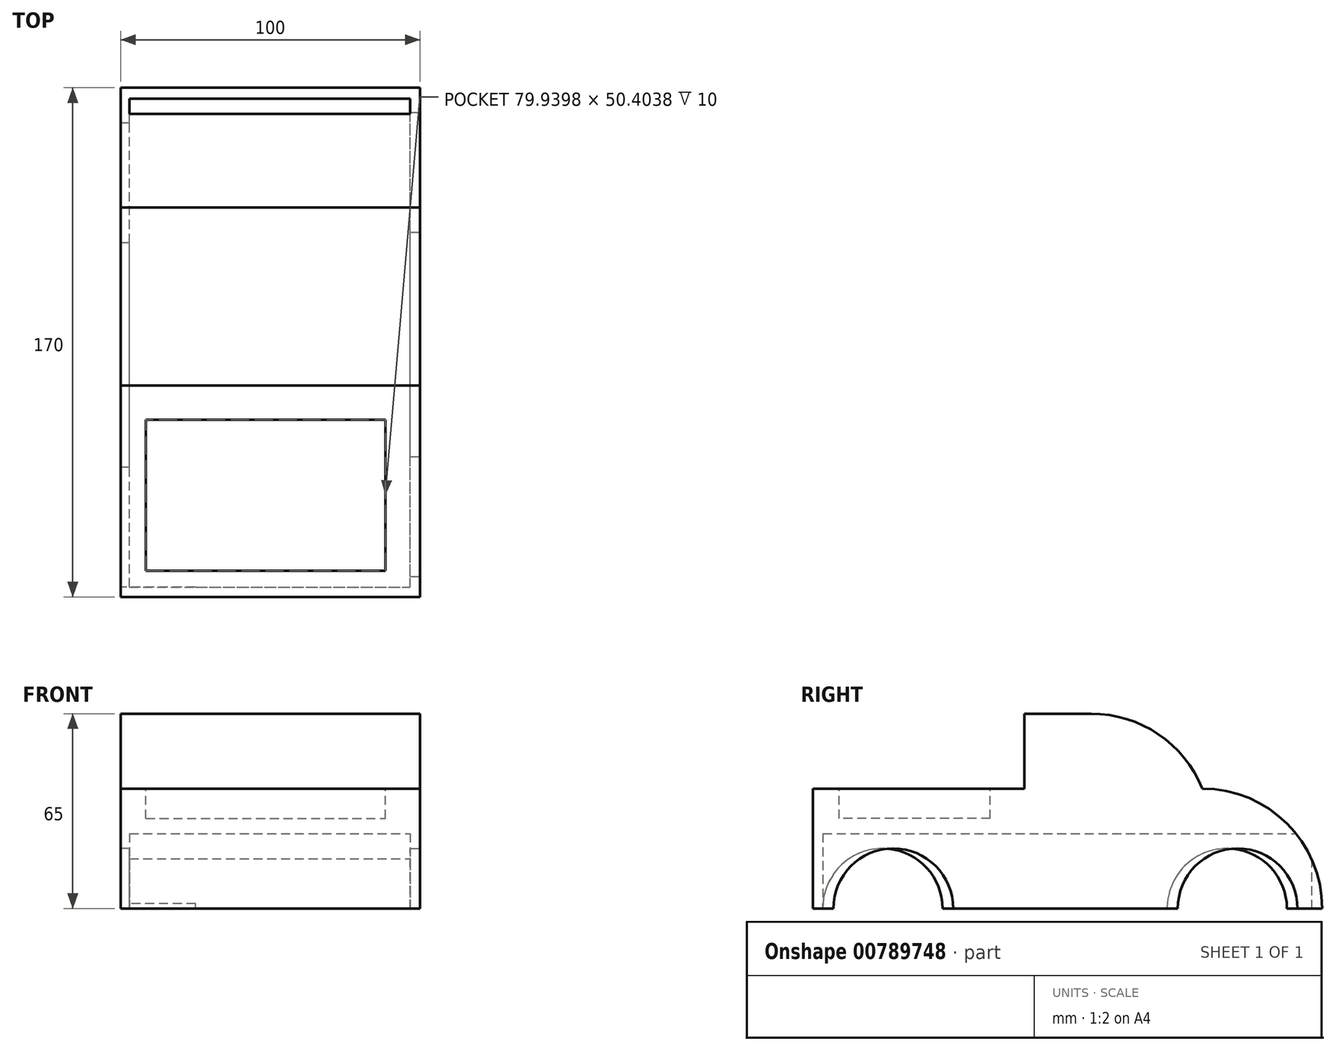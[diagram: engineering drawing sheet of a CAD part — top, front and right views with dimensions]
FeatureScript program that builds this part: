
annotation { "Feature Type Name" : "Feature", "Feature Type Description" : "" }
export const myFeature = defineFeature(function(context is Context, id is Id, definition is map)
    precondition{}
    {
        {
            var Q0;
            Q0=qCreatedBy(makeId("Top.planeOp"),FACE);
            var sketch = newSketch(context, id + "F0", { "sketchPlane" : qUnion([Q0])});
            skLineSegment(sketch, "E0.bottom", {"start": v(-50, 88.78) * mm, "end": v(50, 88.78) * mm});
            skLineSegment(sketch, "E0.top", {"start": v(-50, -81.22) * mm, "end": v(50, -81.22) * mm});
            skLineSegment(sketch, "E0.left", {"start": v(-50, 88.78) * mm, "end": v(-50, -81.22) * mm});
            skLineSegment(sketch, "E0.right", {"start": v(50, 88.78) * mm, "end": v(50, -81.22) * mm});
            skSolve(sketch);
        }
        {
            var Q0;
            Q0=makeQuery(id+"F0.imprint","IMPRINT",FACE,{"disambiguationData":[TD([[makeQuery(id+"F0.imprint","IMPRINT",EDGE,{"derivedFrom":sQuery(id+"F0.wireOp",EDGE,"E0.bottom")}),-1.0]])]});
            extrude(context, id + "F1", {"entities" : qUnion([Q0]), "depth" : 40 * mm, "offsetDistance" : 25 * mm});
        }
        {
            var Q0;
            Q0=makeQuery(id+"F1.opExtrude","CAP_EDGE",EDGE,{"disambiguationData":[OSD([sQuery(id+"F0.wireOp",EDGE,"E0.bottom")])],"isStart":false});
            fillet(context, id + "F2", {"entities" : qUnion([Q0]), "radius" : 40 * mm, "tangentPropagation" : true, "allowEdgeOverflow" : false});
        }
        {
            var Q0;
            Q0=makeQuery(id+"F1.opExtrude","CAP_FACE",FACE,{"disambiguationData":[OSD([sQuery(id+"F0.wireOp",EDGE,"E0.bottom"),sQuery(id+"F0.wireOp",EDGE,"E0.top"),sQuery(id+"F0.wireOp",EDGE,"E0.left"),sQuery(id+"F0.wireOp",EDGE,"E0.right")])],"isStart":false});
            var sketch = newSketch(context, id + "F3", { "sketchPlane" : qUnion([Q0])});
            skLineSegment(sketch, "E1.bottom", {"start": v(-50, 48.78) * mm, "end": v(50, 48.78) * mm});
            skLineSegment(sketch, "E1.top", {"start": v(-50, -10.63) * mm, "end": v(50, -10.63) * mm});
            skLineSegment(sketch, "E1.left", {"start": v(-50, 48.78) * mm, "end": v(-50, -10.63) * mm});
            skLineSegment(sketch, "E1.right", {"start": v(50, 48.78) * mm, "end": v(50, -10.63) * mm});
            skSolve(sketch);
        }
        {
            var Q0;
            Q0=makeQuery(id+"F3.imprint","IMPRINT",FACE,{"disambiguationData":[TD([[makeQuery(id+"F3.imprint","IMPRINT",EDGE,{"derivedFrom":sQuery(id+"F3.wireOp",EDGE,"E1.bottom")}),1.0]])]});
            extrude(context, id + "F4", {"entities" : qUnion([Q0]), "operationType" : NewBodyOperationType.ADD, "depth" : 25 * mm, "offsetDistance" : 25 * mm});
        }
        {
            var Q0;
            Q0=makeQuery(id+"F4.opExtrude","CAP_EDGE",EDGE,{"disambiguationData":[OSD([sQuery(id+"F3.wireOp",EDGE,"E1.bottom")])],"isStart":false});
            fillet(context, id + "F5", {"entities" : qUnion([Q0]), "radius" : 40 * mm, "tangentPropagation" : true, "allowEdgeOverflow" : false});
        }
        {
            var Q0;
            Q0=makeQuery(id+"F4.boolean.opBoolean","MERGE",FACE,{"derivedFrom":[makeQuery(id+"F1.opExtrude","SWEPT_FACE",FACE,{"disambiguationData":[OSD([sQuery(id+"F0.wireOp",EDGE,"E0.right")])]}),makeQuery(id+"F4.opExtrude","SWEPT_FACE",FACE,{"disambiguationData":[OSD([sQuery(id+"F3.wireOp",EDGE,"E1.right")])]})]});
            var sketch = newSketch(context, id + "F6", { "sketchPlane" : qUnion([Q0])});
            skCircle(sketch, "E2", {"center": v(-54.43, 0) * mm, "radius": 20 * mm});
            skCircle(sketch, "E3", {"center": v(60.57, 0) * mm, "radius": 20 * mm});
            skSolve(sketch);
        }
        {
            var Q0;
            {var subQ0=sQuery(id+"F6.wireOp",EDGE,"E2");var subQ1=makeQuery(id+"F1.opExtrude","CAP_EDGE",EDGE,{"disambiguationData":[OSD([sQuery(id+"F0.wireOp",EDGE,"E0.right")])],"isStart":true});var subQ2=makeQuery(id+"F6.imprint","INTERSECT",VERTEX,{"disambiguationData":[OD(0.0)],"derivedFrom":[subQ1,subQ0]});Q0=makeQuery(id+"F6.imprint","IMPRINT",FACE,{"disambiguationData":[TD([[makeQuery(id+"F6.imprint","IMPRINT",EDGE,{"disambiguationData":[TD([[subQ2,1.0]])],"derivedFrom":subQ0}),1.0]])]});}
            var Q1;
            {var subQ0=sQuery(id+"F6.wireOp",EDGE,"E3");var subQ1=makeQuery(id+"F1.opExtrude","CAP_EDGE",EDGE,{"disambiguationData":[OSD([sQuery(id+"F0.wireOp",EDGE,"E0.right")])],"isStart":true});var subQ2=makeQuery(id+"F6.imprint","INTERSECT",VERTEX,{"disambiguationData":[OD(0.0)],"derivedFrom":[subQ1,subQ0]});Q1=makeQuery(id+"F6.imprint","IMPRINT",FACE,{"disambiguationData":[TD([[makeQuery(id+"F6.imprint","IMPRINT",EDGE,{"disambiguationData":[TD([[subQ2,-1.0]])],"derivedFrom":subQ0}),1.0]])]});}
            extrude(context, id + "F7", {"entities" : qUnion([Q0, Q1]), "operationType" : NewBodyOperationType.REMOVE, "oppositeDirection" : true, "depth" : 25 * mm, "offsetDistance" : 25 * mm});
        }
        {
            var Q0;
            Q0=makeQuery(id+"F1.opExtrude","CAP_FACE",FACE,{"disambiguationData":[OSD([sQuery(id+"F0.wireOp",EDGE,"E0.bottom"),sQuery(id+"F0.wireOp",EDGE,"E0.top"),sQuery(id+"F0.wireOp",EDGE,"E0.left"),sQuery(id+"F0.wireOp",EDGE,"E0.right")])],"isStart":true});
            var sketch = newSketch(context, id + "F8", { "sketchPlane" : qUnion([Q0])});
            skLineSegment(sketch, "E4.bottom", {"start": v(-47.03, 77.92) * mm, "end": v(46.71, 77.92) * mm});
            skLineSegment(sketch, "E4.top", {"start": v(-47.03, -85.17) * mm, "end": v(46.71, -85.17) * mm});
            skLineSegment(sketch, "E4.left", {"start": v(-47.03, 77.92) * mm, "end": v(-47.03, -85.17) * mm});
            skLineSegment(sketch, "E4.right", {"start": v(46.71, 77.92) * mm, "end": v(46.71, -85.17) * mm});
            skSolve(sketch);
        }
        {
            var Q0;
            Q0 = qSketchRegion(id + "F8", true);
            extrude(context, id + "F9", {"entities" : qUnion([Q0]), "operationType" : NewBodyOperationType.REMOVE, "oppositeDirection" : true, "depth" : 25 * mm, "offsetDistance" : 25 * mm});
        }
        {
            var Q0;
            Q0=makeQuery(id+"F4.boolean.opBoolean","MERGE",FACE,{"derivedFrom":[makeQuery(id+"F1.opExtrude","SWEPT_FACE",FACE,{"disambiguationData":[OSD([sQuery(id+"F0.wireOp",EDGE,"E0.left")])]}),makeQuery(id+"F4.opExtrude","SWEPT_FACE",FACE,{"disambiguationData":[OSD([sQuery(id+"F3.wireOp",EDGE,"E1.left")])]})]});
            var sketch = newSketch(context, id + "F10", { "sketchPlane" : qUnion([Q0])});
            skCircle(sketch, "E5", {"center": v(-57.01, 0) * mm, "radius": 20 * mm});
            skCircle(sketch, "E6", {"center": v(57.99, 0) * mm, "radius": 20 * mm});
            skSolve(sketch);
        }
        {
            var Q0;
            {var subQ0=sQuery(id+"F10.wireOp",EDGE,"E5");var subQ1=makeQuery(id+"F1.opExtrude","CAP_EDGE",EDGE,{"disambiguationData":[OSD([sQuery(id+"F0.wireOp",EDGE,"E0.left")])],"isStart":true});var subQ2=makeQuery(id+"F10.imprint","INTERSECT",VERTEX,{"disambiguationData":[OD(0.0)],"derivedFrom":[subQ1,subQ0]});Q0=makeQuery(id+"F10.imprint","IMPRINT",FACE,{"disambiguationData":[TD([[makeQuery(id+"F10.imprint","IMPRINT",EDGE,{"disambiguationData":[TD([[subQ2,-1.0]])],"derivedFrom":subQ0}),1.0]])]});}
            var Q1;
            {var subQ0=sQuery(id+"F10.wireOp",EDGE,"E6");var subQ1=makeQuery(id+"F1.opExtrude","CAP_EDGE",EDGE,{"disambiguationData":[OSD([sQuery(id+"F0.wireOp",EDGE,"E0.left")])],"isStart":true});var subQ2=makeQuery(id+"F10.imprint","INTERSECT",VERTEX,{"disambiguationData":[OD(0.0)],"derivedFrom":[subQ1,subQ0]});Q1=makeQuery(id+"F10.imprint","IMPRINT",FACE,{"disambiguationData":[TD([[makeQuery(id+"F10.imprint","IMPRINT",EDGE,{"disambiguationData":[TD([[subQ2,1.0]])],"derivedFrom":subQ0}),1.0]])]});}
            var Q2;
            {var subQ0=sQuery(id+"F10.wireOp",EDGE,"E5");var subQ1=makeQuery(id+"F1.opExtrude","CAP_EDGE",EDGE,{"disambiguationData":[OSD([sQuery(id+"F0.wireOp",EDGE,"E0.left")])],"isStart":true});var subQ2=makeQuery(id+"F10.imprint","INTERSECT",VERTEX,{"disambiguationData":[OD(0.0)],"derivedFrom":[subQ1,subQ0]});Q2=makeQuery(id+"F10.imprint","IMPRINT",FACE,{"disambiguationData":[TD([[makeQuery(id+"F10.imprint","IMPRINT",EDGE,{"disambiguationData":[TD([[subQ2,1.0]])],"derivedFrom":subQ0}),1.0]])]});}
            var Q3;
            {var subQ0=sQuery(id+"F10.wireOp",EDGE,"E6");var subQ1=makeQuery(id+"F1.opExtrude","CAP_EDGE",EDGE,{"disambiguationData":[OSD([sQuery(id+"F0.wireOp",EDGE,"E0.left")])],"isStart":true});var subQ2=makeQuery(id+"F10.imprint","INTERSECT",VERTEX,{"disambiguationData":[OD(0.0)],"derivedFrom":[subQ1,subQ0]});Q3=makeQuery(id+"F10.imprint","IMPRINT",FACE,{"disambiguationData":[TD([[makeQuery(id+"F10.imprint","IMPRINT",EDGE,{"disambiguationData":[TD([[subQ2,-1.0]])],"derivedFrom":subQ0}),1.0]])]});}
            extrude(context, id + "F11", {"entities" : qUnion([Q0, Q1, Q2, Q3]), "operationType" : NewBodyOperationType.REMOVE, "oppositeDirection" : true, "depth" : 25 * mm, "offsetDistance" : 25 * mm});
        }
        {
            var Q0;
            Q0=makeQuery(id+"F1.opExtrude","CAP_FACE",FACE,{"disambiguationData":[OSD([sQuery(id+"F0.wireOp",EDGE,"E0.bottom"),sQuery(id+"F0.wireOp",EDGE,"E0.top"),sQuery(id+"F0.wireOp",EDGE,"E0.left"),sQuery(id+"F0.wireOp",EDGE,"E0.right")])],"isStart":false});
            var sketch = newSketch(context, id + "F12", { "sketchPlane" : qUnion([Q0])});
            skLineSegment(sketch, "E7.bottom", {"start": v(-41.58, -22.06) * mm, "end": v(38.36, -22.06) * mm});
            skLineSegment(sketch, "E7.top", {"start": v(-41.58, -72.46) * mm, "end": v(38.36, -72.46) * mm});
            skLineSegment(sketch, "E7.left", {"start": v(-41.58, -22.06) * mm, "end": v(-41.58, -72.46) * mm});
            skLineSegment(sketch, "E7.right", {"start": v(38.36, -22.06) * mm, "end": v(38.36, -72.46) * mm});
            skSolve(sketch);
        }
        {
            var Q0;
            Q0=makeQuery(id+"F12.imprint","IMPRINT",FACE,{"disambiguationData":[TD([[makeQuery(id+"F12.imprint","IMPRINT",EDGE,{"derivedFrom":sQuery(id+"F12.wireOp",EDGE,"E7.bottom")}),-1.0]])]});
            extrude(context, id + "F13", {"entities" : qUnion([Q0]), "operationType" : NewBodyOperationType.REMOVE, "oppositeDirection" : true, "depth" : 10 * mm, "offsetDistance" : 25 * mm});
        }
    });
